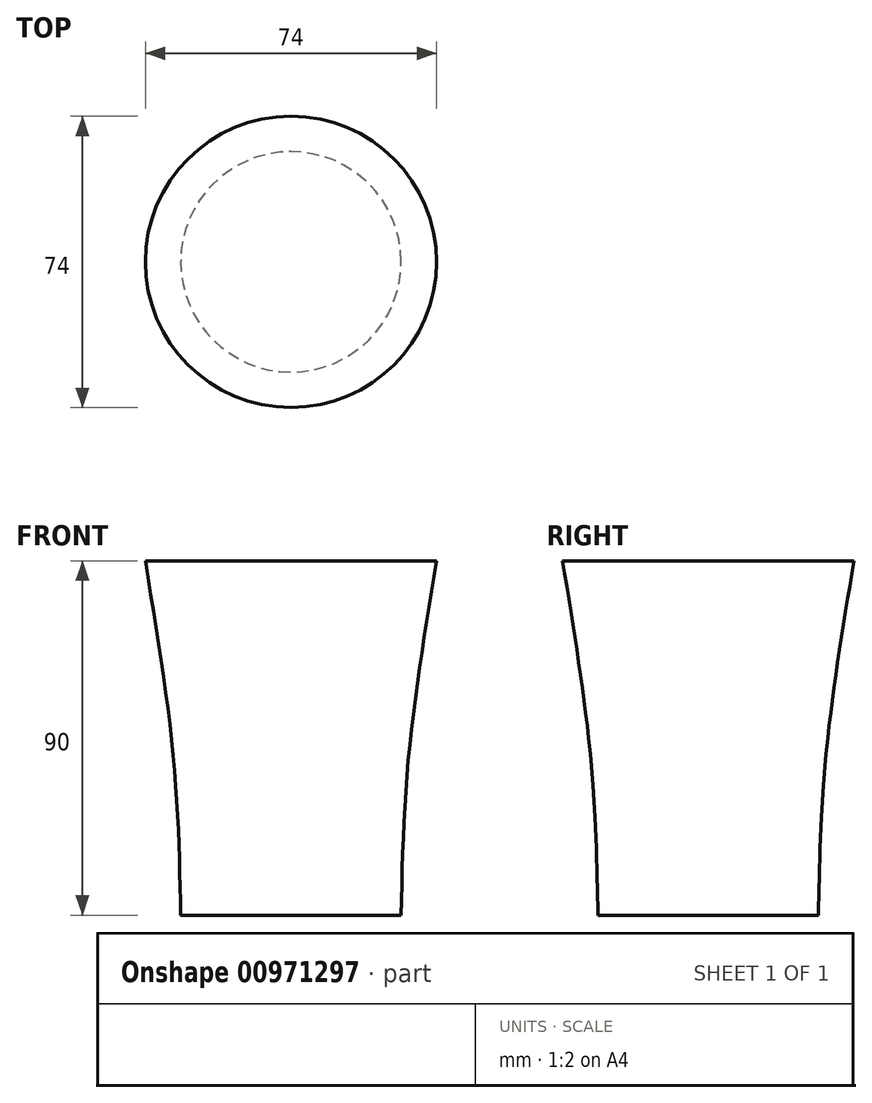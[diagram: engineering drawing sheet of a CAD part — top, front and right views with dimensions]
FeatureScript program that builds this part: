
annotation { "Feature Type Name" : "Feature", "Feature Type Description" : "" }
export const myFeature = defineFeature(function(context is Context, id is Id, definition is map)
    precondition{}
    {
        {
            var Q0;
            Q0=qCreatedBy(makeId("Front.planeOp"),FACE);
            var sketch = newSketch(context, id + "F0", { "sketchPlane" : qUnion([Q0])});
            skLineSegment(sketch, "E0", {"start": v(28, 0) * mm, "end": v(0, 0) * mm});
            skLineSegment(sketch, "E1", {"start": v(0, 0) * mm, "end": v(0, 90) * mm});
            skLineSegment(sketch, "E2", {"start": v(0, 90) * mm, "end": v(37, 90) * mm});
            skFitSpline(sketch, "E3", {"points": [v(28, 0) * mm, v(29.85, 39.93) * mm, v(37, 90) * mm], "startDerivative": vector(1.68, 82.56) * mm, "endDerivative": vector(16.04, 97.16) * mm});
            skSolve(sketch);
        }
        {
            var Q0;
            Q0=makeQuery(id+"F0.imprint","IMPRINT",FACE,{"disambiguationData":[TD([[makeQuery(id+"F0.imprint","IMPRINT",EDGE,{"derivedFrom":sQuery(id+"F0.wireOp",EDGE,"E0")}),-1.0]])]});
            var Q1;
            Q1=sQuery(id+"F0.wireOp",EDGE,"E1");
            revolve(context, id + "F1", {"surfaceOperationType" : NewSurfaceOperationType.NEW, "entities" : qUnion([Q0]), "axis" : qUnion([Q1]), "revolveType" : RevolveType.FULL});
        }
    });
